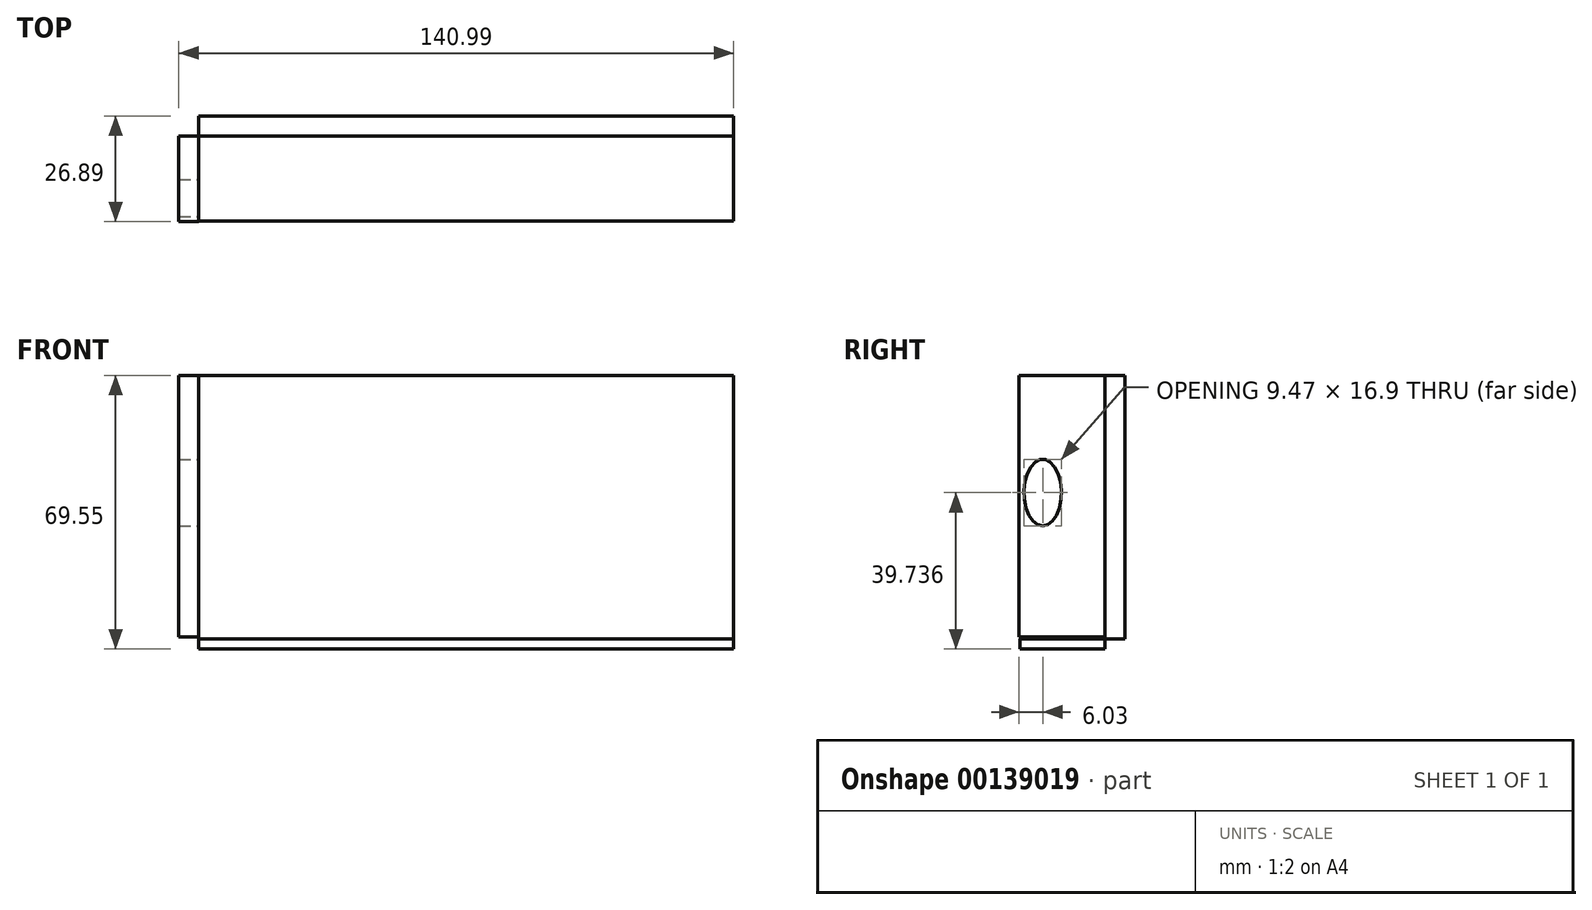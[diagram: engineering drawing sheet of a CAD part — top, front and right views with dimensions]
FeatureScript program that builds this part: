
annotation { "Feature Type Name" : "Feature", "Feature Type Description" : "" }
export const myFeature = defineFeature(function(context is Context, id is Id, definition is map)
    precondition{}
    {
        {
            var Q0;
            Q0=qCreatedBy(makeId("Front.planeOp"),FACE);
            var sketch = newSketch(context, id + "F0", { "sketchPlane" : qUnion([Q0])});
            skLineSegment(sketch, "E0.bottom", {"start": v(-70.3, 33.35) * mm, "end": v(65.6, 33.35) * mm});
            skLineSegment(sketch, "E0.top", {"start": v(-70.3, -33.66) * mm, "end": v(65.6, -33.66) * mm});
            skLineSegment(sketch, "E0.left", {"start": v(-70.3, 33.35) * mm, "end": v(-70.3, -33.66) * mm});
            skLineSegment(sketch, "E0.right", {"start": v(65.6, 33.35) * mm, "end": v(65.6, -33.66) * mm});
            skSolve(sketch);
        }
        {
            var Q0;
            Q0=makeQuery(id+"F0.imprint","IMPRINT",FACE,{"disambiguationData":[TD([[makeQuery(id+"F0.imprint","IMPRINT",EDGE,{"derivedFrom":sQuery(id+"F0.wireOp",EDGE,"E0.bottom")}),-1.0]])]});
            extrude(context, id + "F1", {"entities" : qUnion([Q0]), "depth" : 5.08 * mm});
        }
        {
            var Q0;
            Q0=makeQuery(id+"F1.opExtrude","SWEPT_FACE",FACE,{"disambiguationData":[OSD([sQuery(id+"F0.wireOp",EDGE,"E0.left")])]});
            var sketch = newSketch(context, id + "F2", { "sketchPlane" : qUnion([Q0])});
            skLineSegment(sketch, "E1.bottom", {"start": v(0, 33.35) * mm, "end": v(26.9, 33.35) * mm});
            skLineSegment(sketch, "E1.top", {"start": v(0, -33.15) * mm, "end": v(26.9, -33.15) * mm});
            skLineSegment(sketch, "E1.left", {"start": v(0, 33.35) * mm, "end": v(0, -33.15) * mm});
            skLineSegment(sketch, "E1.right", {"start": v(26.9, 33.35) * mm, "end": v(26.9, -33.15) * mm});
            skEllipse(sketch, "E2", {"center": v(20.86, 3.54) * mm, "majorRadius": 8.45 * mm, "minorRadius": 4.73 * mm, "majorAxis": v(0, -1)});
            skSolve(sketch);
        }
        {
            var Q0;
            {var subQ3=sQuery(id+"F2.wireOp",EDGE,"E1.right");Q0=makeQuery(id+"F2.imprint","IMPRINT",FACE,{"disambiguationData":[TD([[makeQuery(id+"F2.imprint","IMPRINT",EDGE,{"derivedFrom":subQ3}),-1.0]])]});}
            extrude(context, id + "F3", {"entities" : qUnion([Q0]), "depth" : 5.08 * mm});
        }
        {
            var Q0;
            Q0=sQuery(id+"F2.wireOp",EDGE,"E2");
            extrude(context, id + "F4", {"bodyType" : ToolBodyType.SURFACE, "surfaceEntities" : qUnion([Q0]), "oppositeDirection" : true, "depth" : 0.25 * mm});
        }
        {
            var Q0;
            Q0=makeQuery(id+"F1.opExtrude","SWEPT_FACE",FACE,{"disambiguationData":[OSD([sQuery(id+"F0.wireOp",EDGE,"E0.top")])]});
            var sketch = newSketch(context, id + "F5", { "sketchPlane" : qUnion([Q0])});
            skLineSegment(sketch, "E3.bottom", {"start": v(-70.3, 5.08) * mm, "end": v(65.6, 5.08) * mm});
            skLineSegment(sketch, "E3.top", {"start": v(-70.3, 26.66) * mm, "end": v(65.6, 26.66) * mm});
            skLineSegment(sketch, "E3.left", {"start": v(-70.3, 5.08) * mm, "end": v(-70.3, 26.66) * mm});
            skLineSegment(sketch, "E3.right", {"start": v(65.6, 5.08) * mm, "end": v(65.6, 26.66) * mm});
            skSolve(sketch);
        }
        {
            var Q0;
            Q0=makeQuery(id+"F5.imprint","IMPRINT",FACE,{"disambiguationData":[TD([[makeQuery(id+"F5.imprint","IMPRINT",EDGE,{"derivedFrom":sQuery(id+"F5.wireOp",EDGE,"E3.bottom")}),1.0]])]});
            extrude(context, id + "F6", {"entities" : qUnion([Q0]), "depth" : 2.54 * mm});
        }
    });
